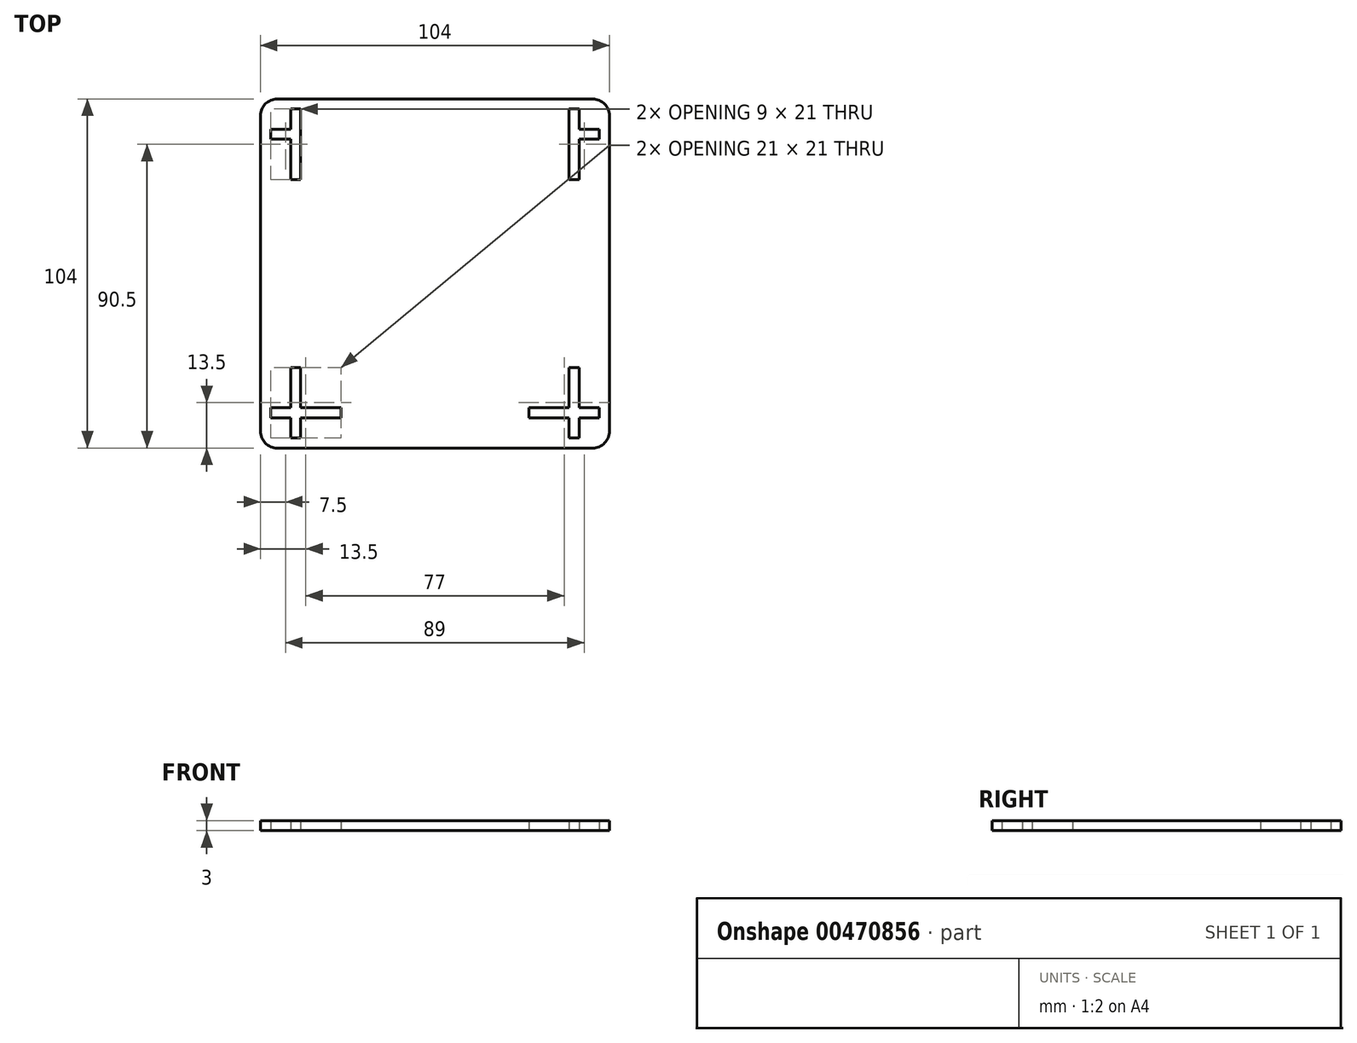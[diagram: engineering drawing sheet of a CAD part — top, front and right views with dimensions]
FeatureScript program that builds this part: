
annotation { "Feature Type Name" : "Feature", "Feature Type Description" : "" }
export const myFeature = defineFeature(function(context is Context, id is Id, definition is map)
    precondition{}
    {
        {
            assignVariable(context, id + "F0", {"name" : "WoodWidth", "anyValue" : 3});
        }
        {
            var Q0;
            Q0=qCreatedBy(makeId("Top.planeOp"),FACE);
            var sketch = newSketch(context, id + "F1", { "sketchPlane" : qUnion([Q0])});
            skLineSegment(sketch, "E0.bottom", {"start": v(52, -52) * mm, "end": v(-52, -52) * mm});
            skLineSegment(sketch, "E0.top", {"start": v(52, 52) * mm, "end": v(-52, 52) * mm});
            skLineSegment(sketch, "E0.left", {"start": v(52, -52) * mm, "end": v(52, 52) * mm});
            skLineSegment(sketch, "E0.right", {"start": v(-52, -52) * mm, "end": v(-52, 52) * mm});
            skPoint(sketch, "E0.middle", {"position": v(0, 0) * mm});
            skLineSegment(sketch, "E1.bottom", {"start": v(40, -40) * mm, "end": v(-40, -40) * mm});
            skLineSegment(sketch, "E1.top", {"start": v(40, 40) * mm, "end": v(-40, 40) * mm});
            skLineSegment(sketch, "E1.left", {"start": v(40, -40) * mm, "end": v(40, 40) * mm});
            skLineSegment(sketch, "E1.right", {"start": v(-40, -40) * mm, "end": v(-40, 40) * mm});
            skLineSegment(sketch, "E2.bottom", {"start": v(-40, -28) * mm, "end": v(-43, -28) * mm});
            skLineSegment(sketch, "E2.top", {"start": v(-40, -49) * mm, "end": v(-43, -49) * mm});
            skLineSegment(sketch, "E2.left", {"start": v(-40, -28) * mm, "end": v(-40, -49) * mm});
            skLineSegment(sketch, "E2.right", {"start": v(-43, -28) * mm, "end": v(-43, -49) * mm});
            skLineSegment(sketch, "E3.bottom", {"start": v(-28, -40) * mm, "end": v(-49, -40) * mm});
            skLineSegment(sketch, "E3.top", {"start": v(-28, -43) * mm, "end": v(-49, -43) * mm});
            skLineSegment(sketch, "E3.left", {"start": v(-28, -40) * mm, "end": v(-28, -43) * mm});
            skLineSegment(sketch, "E3.right", {"start": v(-49, -40) * mm, "end": v(-49, -43) * mm});
            skLineSegment(sketch, "E4.MirrorCS", {"start": v(43, -28) * mm, "end": v(43, -49) * mm});
            skLineSegment(sketch, "E5.MirrorCS", {"start": v(40, -28) * mm, "end": v(43, -28) * mm});
            skLineSegment(sketch, "E6.MirrorCS", {"start": v(40, -28) * mm, "end": v(40, -49) * mm});
            skLineSegment(sketch, "E7.MirrorCS", {"start": v(49, -40) * mm, "end": v(49, -43) * mm});
            skLineSegment(sketch, "E8.MirrorCS", {"start": v(28, -43) * mm, "end": v(49, -43) * mm});
            skLineSegment(sketch, "E9.MirrorCS", {"start": v(28, -40) * mm, "end": v(49, -40) * mm});
            skLineSegment(sketch, "E10.MirrorCS", {"start": v(40, -49) * mm, "end": v(43, -49) * mm});
            skLineSegment(sketch, "E11.MirrorCS", {"start": v(28, -40) * mm, "end": v(28, -43) * mm});
            skLineSegment(sketch, "E12.MirrorCS", {"start": v(-40, 28) * mm, "end": v(-43, 28) * mm});
            skLineSegment(sketch, "E13.MirrorCS", {"start": v(-43, 28) * mm, "end": v(-43, 49) * mm});
            skLineSegment(sketch, "E14.MirrorCS", {"start": v(-40, 49) * mm, "end": v(-43, 49) * mm});
            skLineSegment(sketch, "E15.MirrorCS", {"start": v(-40, 28) * mm, "end": v(-40, 49) * mm});
            skLineSegment(sketch, "E16.MirrorCS", {"start": v(40, 28) * mm, "end": v(43, 28) * mm});
            skLineSegment(sketch, "E17.MirrorCS", {"start": v(43, 28) * mm, "end": v(43, 49) * mm});
            skLineSegment(sketch, "E18.MirrorCS", {"start": v(40, 49) * mm, "end": v(43, 49) * mm});
            skLineSegment(sketch, "E19.MirrorCS", {"start": v(40, 28) * mm, "end": v(40, 49) * mm});
            skLineSegment(sketch, "E20.bottom", {"start": v(-40, 40) * mm, "end": v(-49, 40) * mm});
            skLineSegment(sketch, "E20.top", {"start": v(-40, 43) * mm, "end": v(-49, 43) * mm});
            skLineSegment(sketch, "E20.left", {"start": v(-40, 40) * mm, "end": v(-40, 43) * mm});
            skLineSegment(sketch, "E20.right", {"start": v(-49, 40) * mm, "end": v(-49, 43) * mm});
            skLineSegment(sketch, "E21.bottom", {"start": v(40, 40) * mm, "end": v(49, 40) * mm});
            skLineSegment(sketch, "E21.top", {"start": v(40, 43) * mm, "end": v(49, 43) * mm});
            skLineSegment(sketch, "E21.left", {"start": v(40, 40) * mm, "end": v(40, 43) * mm});
            skLineSegment(sketch, "E21.right", {"start": v(49, 40) * mm, "end": v(49, 43) * mm});
            skSolve(sketch);
        }
        {
            var Q0;
            Q0=makeQuery(id+"F1.imprint","IMPRINT",FACE,{"disambiguationData":[TD([[makeQuery(id+"F1.imprint","IMPRINT",EDGE,{"derivedFrom":sQuery(id+"F1.wireOp",EDGE,"E0.bottom")}),-1.0]])]});
            var Q1;
            {var subQ7=sQuery(id+"F1.wireOp",EDGE,"E1.bottom");Q1=makeQuery(id+"F1.imprint","IMPRINT",FACE,{"disambiguationData":[TD([[makeQuery(id+"F1.imprint","IMPRINT",EDGE,{"derivedFrom":subQ7}),-1.0]])]});}
            extrude(context, id + "F2", {"entities" : qUnion([Q0, Q1]), "depth" : (getVariable(context, 'WoodWidth')) * mm});
        }
        {
            var Q0;
            Q0=makeQuery(id+"F2.opExtrude","SWEPT_EDGE",EDGE,{"disambiguationData":[OSD([sQuery(id+"F1.wireOp",EDGE,"E0.bottom"),sQuery(id+"F1.wireOp",EDGE,"E0.right")])]});
            var Q1;
            Q1=makeQuery(id+"F2.opExtrude","SWEPT_EDGE",EDGE,{"disambiguationData":[OSD([sQuery(id+"F1.wireOp",EDGE,"E0.top"),sQuery(id+"F1.wireOp",EDGE,"E0.right")])]});
            var Q2;
            Q2=makeQuery(id+"F2.opExtrude","SWEPT_EDGE",EDGE,{"disambiguationData":[OSD([sQuery(id+"F1.wireOp",EDGE,"E0.bottom"),sQuery(id+"F1.wireOp",EDGE,"E0.left")])]});
            var Q3;
            Q3=makeQuery(id+"F2.opExtrude","SWEPT_EDGE",EDGE,{"disambiguationData":[OSD([sQuery(id+"F1.wireOp",EDGE,"E0.top"),sQuery(id+"F1.wireOp",EDGE,"E0.left")])]});
            fillet(context, id + "F3", {"entities" : qUnion([Q0, Q1, Q2, Q3]), "radius" : 5 * mm, "tangentPropagation" : true, "allowEdgeOverflow" : false});
        }
    });
